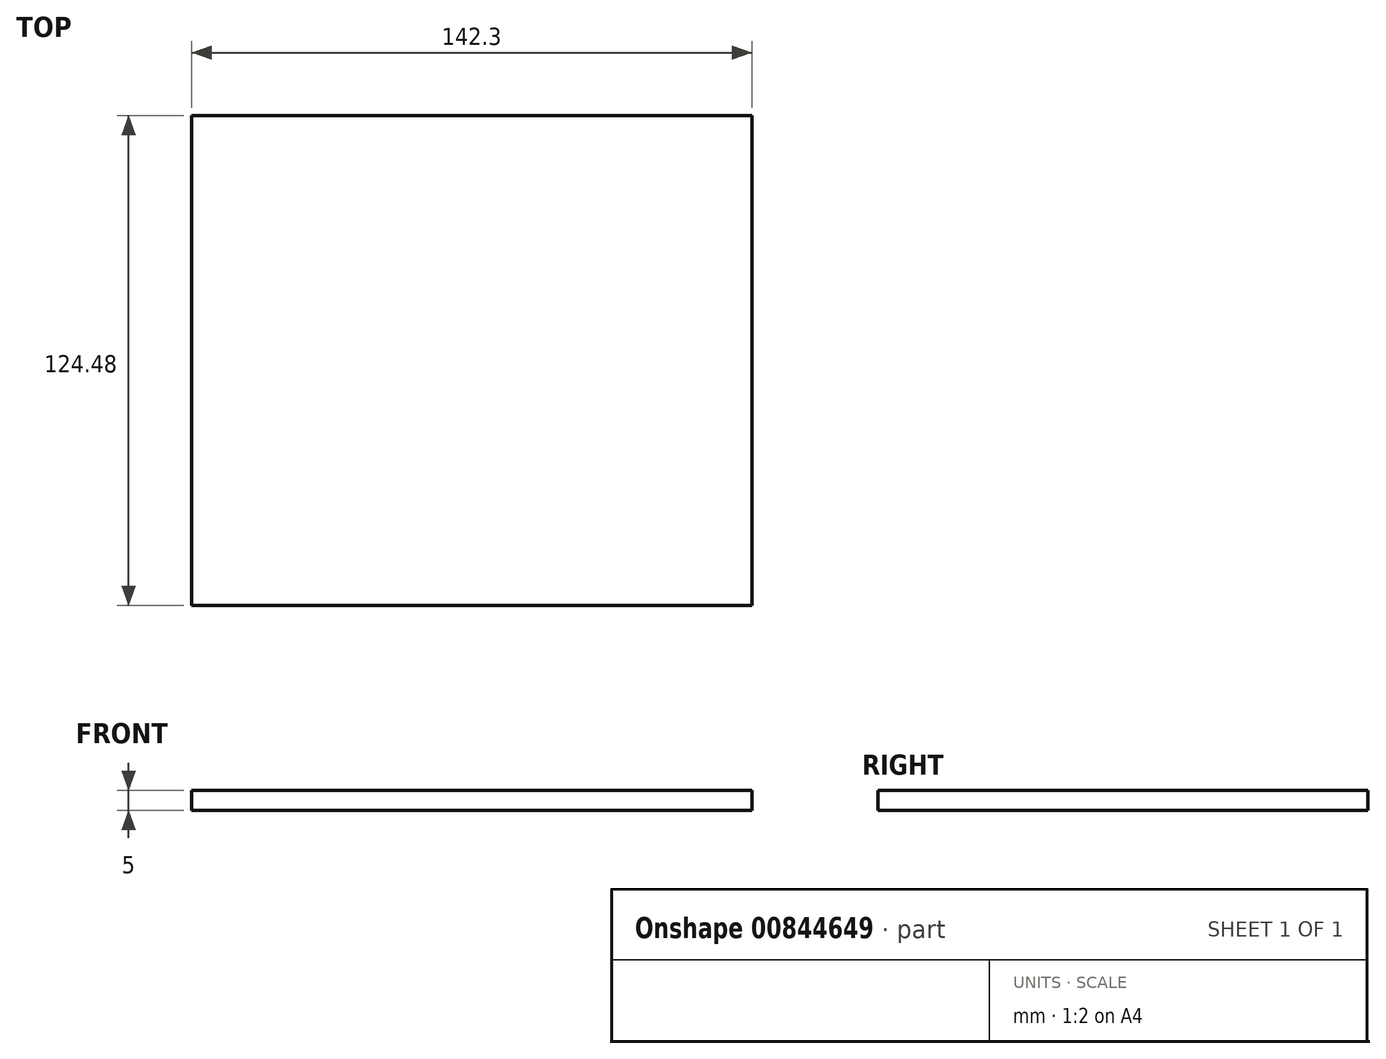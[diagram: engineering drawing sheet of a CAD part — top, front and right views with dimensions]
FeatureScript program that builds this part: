
annotation { "Feature Type Name" : "Feature", "Feature Type Description" : "" }
export const myFeature = defineFeature(function(context is Context, id is Id, definition is map)
    precondition{}
    {
        {
            var Q0;
            Q0=qCreatedBy(makeId("Top.planeOp"),FACE);
            var sketch = newSketch(context, id + "F0", { "sketchPlane" : qUnion([Q0])});
            skLineSegment(sketch, "E0.bottom", {"start": v(-72.25, 62.14) * mm, "end": v(70.05, 62.14) * mm});
            skLineSegment(sketch, "E0.top", {"start": v(-72.25, -62.34) * mm, "end": v(70.05, -62.34) * mm});
            skLineSegment(sketch, "E0.left", {"start": v(-72.25, 62.14) * mm, "end": v(-72.25, -62.34) * mm});
            skLineSegment(sketch, "E0.right", {"start": v(70.05, 62.14) * mm, "end": v(70.05, -62.34) * mm});
            skSolve(sketch);
        }
        {
            var Q0;
            Q0=makeQuery(id+"F0.imprint","IMPRINT",FACE,{"disambiguationData":[TD([[makeQuery(id+"F0.imprint","IMPRINT",EDGE,{"derivedFrom":sQuery(id+"F0.wireOp",EDGE,"E0.bottom")}),-1.0]])]});
            extrude(context, id + "F1", {"entities" : qUnion([Q0]), "depth" : 5 * mm, "offsetDistance" : 25 * mm});
        }
    });
